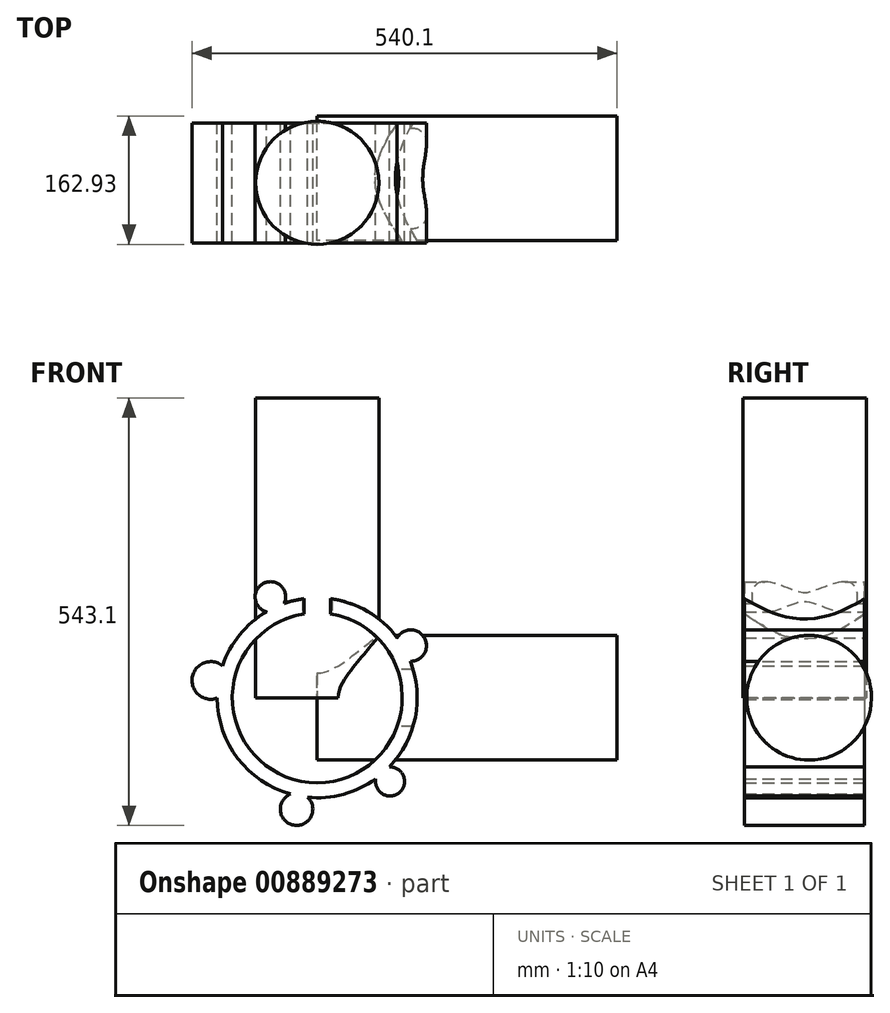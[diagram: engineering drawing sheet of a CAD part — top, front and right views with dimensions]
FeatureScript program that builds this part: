
annotation { "Feature Type Name" : "Feature", "Feature Type Description" : "" }
export const myFeature = defineFeature(function(context is Context, id is Id, definition is map)
    precondition{}
    {
        {
            var Q0;
            Q0=qCreatedBy(makeId("Front.planeOp"),FACE);
            var sketch = newSketch(context, id + "F0", { "sketchPlane" : qUnion([Q0])});
            skCircle(sketch, "E0", {"center": v(0, 0) * mm, "radius": 127 * mm});
            skCircle(sketch, "E1", {"center": v(0, 0) * mm, "radius": 107.95 * mm});
            skSolve(sketch);
        }
        {
            var Q0;
            Q0=makeQuery(id+"F0.imprint","IMPRINT",FACE,{"disambiguationData":[TD([[makeQuery(id+"F0.imprint","IMPRINT",EDGE,{"derivedFrom":sQuery(id+"F0.wireOp",EDGE,"E0")}),1.0]])]});
            extrude(context, id + "F1", {"entities" : qUnion([Q0]), "depth" : 152.4 * mm, "offsetDistance" : 25.4 * mm});
        }
        {
            var Q0;
            Q0=qCreatedBy(makeId("Front.planeOp"),FACE);
            var sketch = newSketch(context, id + "F2", { "sketchPlane" : qUnion([Q0])});
            skCircle(sketch, "E2", {"center": v(118.74, 66.27) * mm, "radius": 19.95 * mm});
            skCircle(sketch, "E3", {"center": v(92.45, -106.4) * mm, "radius": 18.48 * mm});
            skCircle(sketch, "E4", {"center": v(-59.5, 128.02) * mm, "radius": 19.43 * mm});
            skCircle(sketch, "E5", {"center": v(-135.19, 22) * mm, "radius": 23.92 * mm});
            skCircle(sketch, "E6", {"center": v(-26.29, -141.47) * mm, "radius": 20.63 * mm});
            skSolve(sketch);
        }
        {
            var Q0;
            Q0 = qSketchRegion(id + "F2", true);
            extrude(context, id + "F3", {"entities" : qUnion([Q0]), "operationType" : NewBodyOperationType.ADD, "depth" : 152.4 * mm, "offsetDistance" : 25.4 * mm});
        }
        {
            var Q0;
            Q0=qCreatedBy(makeId("Top.planeOp"),FACE);
            var sketch = newSketch(context, id + "F4", { "sketchPlane" : qUnion([Q0])});
            skCircle(sketch, "E7", {"center": v(0, -75.98) * mm, "radius": 78.21 * mm});
            skSolve(sketch);
        }
        {
            var Q0;
            Q0=makeQuery(id+"F4.imprint","IMPRINT",FACE,{"disambiguationData":[TD([[makeQuery(id+"F4.imprint","IMPRINT",EDGE,{"derivedFrom":sQuery(id+"F4.wireOp",EDGE,"E7")}),1.0]])]});
            extrude(context, id + "F5", {"entities" : qUnion([Q0]), "operationType" : NewBodyOperationType.ADD, "depth" : 381 * mm, "offsetDistance" : 25.4 * mm});
        }
        {
            var Q0;
            Q0=qCreatedBy(makeId("Right.planeOp"),FACE);
            var sketch = newSketch(context, id + "F6", { "sketchPlane" : qUnion([Q0])});
            skCircle(sketch, "E8", {"center": v(-70.44, 0) * mm, "radius": 79.18 * mm});
            skSolve(sketch);
        }
        {
            var Q0;
            Q0 = qSketchRegion(id + "F6", true);
            extrude(context, id + "F7", {"entities" : qUnion([Q0]), "operationType" : NewBodyOperationType.ADD, "depth" : 381 * mm, "offsetDistance" : 25.4 * mm});
        }
    });
